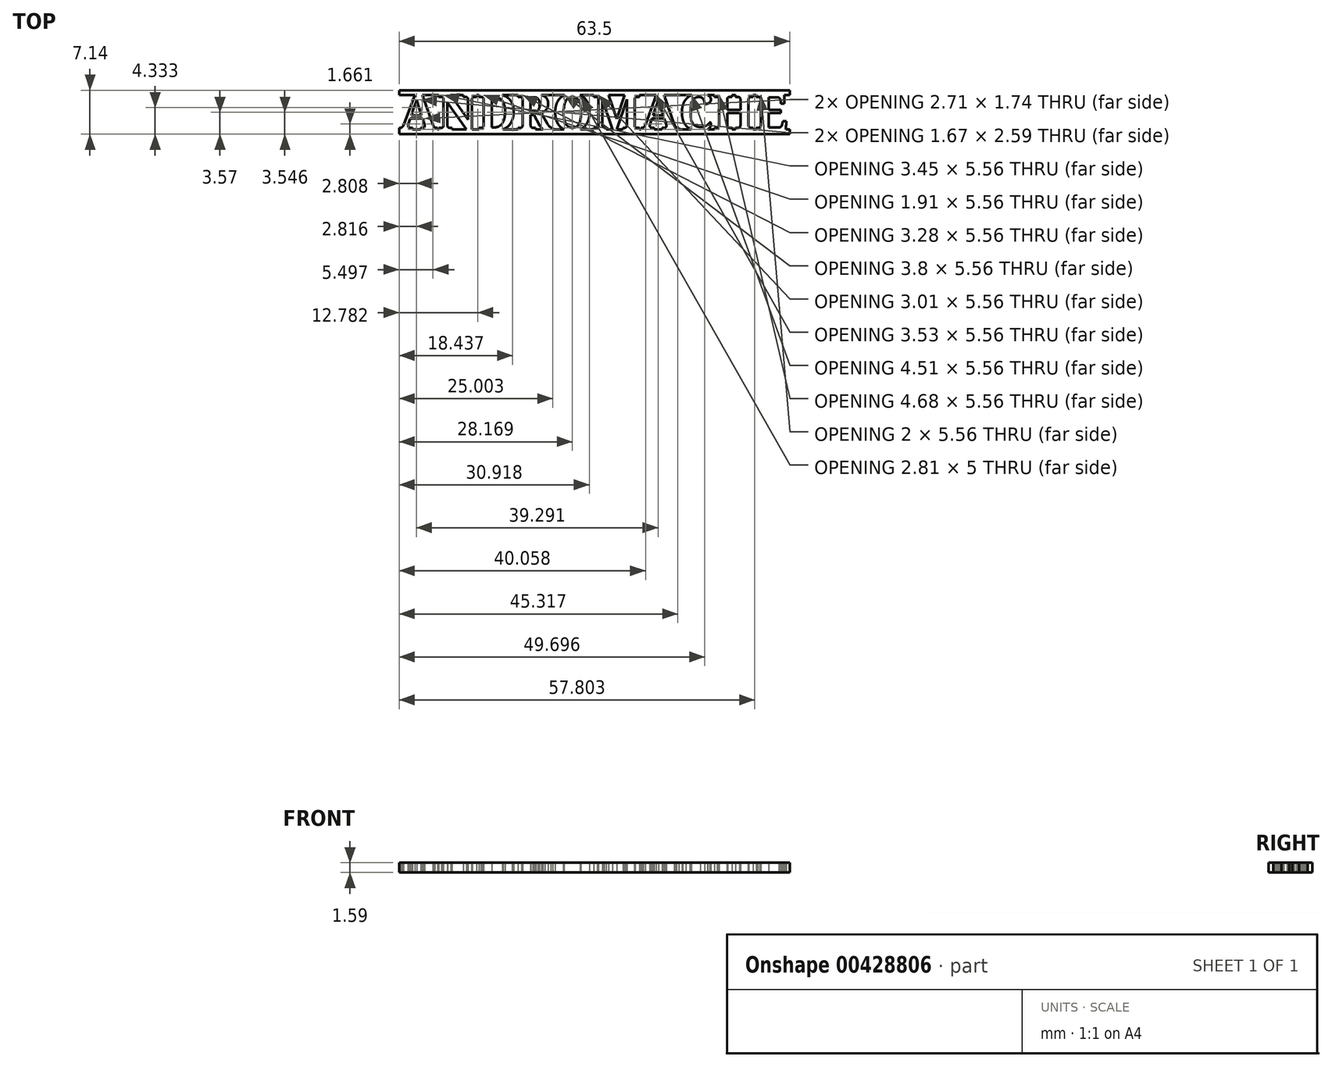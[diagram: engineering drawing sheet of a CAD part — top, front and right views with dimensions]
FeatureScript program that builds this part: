
annotation { "Feature Type Name" : "Feature", "Feature Type Description" : "" }
export const myFeature = defineFeature(function(context is Context, id is Id, definition is map)
    precondition{}
    {
        {
            var Q0;
            Q0=qCreatedBy(makeId("Top.planeOp"),FACE);
            var sketch = newSketch(context, id + "F0", { "sketchPlane" : qUnion([Q0])});
            skText(sketch, "E0", { "text": "ANDROMACHE", "fontName": "NotoSerif-Bold.ttf"});
            skLineSegment(sketch, "E1", {"start": v(31.75, 2.78) * mm, "end": v(31.75, 3.57) * mm});
            skLineSegment(sketch, "E2", {"start": v(31.75, 3.57) * mm, "end": v(-31.75, 3.57) * mm});
            skLineSegment(sketch, "E3", {"start": v(-31.75, 3.57) * mm, "end": v(-31.75, 2.78) * mm});
            skLineSegment(sketch, "E4.bottom", {"start": v(-31.75, -2.78) * mm, "end": v(31.75, -2.78) * mm});
            skLineSegment(sketch, "E4.top", {"start": v(-31.75, -3.57) * mm, "end": v(31.75, -3.57) * mm});
            skLineSegment(sketch, "E4.left", {"start": v(-31.75, -2.78) * mm, "end": v(-31.75, -3.57) * mm});
            skLineSegment(sketch, "E4.right", {"start": v(31.75, -2.78) * mm, "end": v(31.75, -3.57) * mm});
            skLineSegment(sketch, "E5", {"start": v(31.75, 2.78) * mm, "end": v(-31.75, 2.78) * mm});
            const initialGuessF0  = {"E0": [-0.03175, -0.00298, 1, 0, 0.00595]};
            skSetInitialGuess(sketch, initialGuessF0);
            skSolve(sketch);
        }
        {
            var Q0;
            {var subQ43=sQuery(id+"F0.wireOp",EDGE,"E0.sketch_text.stroke-17");Q0=makeQuery(id+"F0.imprint","IMPRINT",FACE,{"disambiguationData":[TD([[makeQuery(id+"F0.imprint","IMPRINT",EDGE,{"derivedFrom":subQ43}),1.0]])]});}
            var Q1;
            {var subQ0=sQuery(id+"F0.wireOp",EDGE,"E0.sketch_text.stroke-78");Q1=makeQuery(id+"F0.imprint","IMPRINT",FACE,{"disambiguationData":[TD([[makeQuery(id+"F0.imprint","IMPRINT",EDGE,{"derivedFrom":subQ0}),-1.0]])]});}
            var Q2;
            {var subQ7=sQuery(id+"F0.wireOp",EDGE,"E0.sketch_text.stroke-47");Q2=makeQuery(id+"F0.imprint","IMPRINT",FACE,{"disambiguationData":[TD([[makeQuery(id+"F0.imprint","IMPRINT",EDGE,{"derivedFrom":subQ7}),-1.0]])]});}
            var Q3;
            {var subQ0=sQuery(id+"F0.wireOp",EDGE,"E0.sketch_text.stroke-69");Q3=makeQuery(id+"F0.imprint","IMPRINT",FACE,{"disambiguationData":[TD([[makeQuery(id+"F0.imprint","IMPRINT",EDGE,{"derivedFrom":subQ0}),-1.0]])]});}
            var Q4;
            Q4=makeQuery(id+"F0.imprint","IMPRINT",FACE,{"disambiguationData":[TD([[makeQuery(id+"F0.imprint","IMPRINT",EDGE,{"derivedFrom":sQuery(id+"F0.wireOp",EDGE,"E0.sketch_text.stroke-0")}),-1.0]])]});
            var Q5;
            {var subQ0=sQuery(id+"F0.wireOp",EDGE,"E0.sketch_text.stroke-17");Q5=makeQuery(id+"F0.imprint","IMPRINT",FACE,{"disambiguationData":[TD([[makeQuery(id+"F0.imprint","IMPRINT",EDGE,{"derivedFrom":subQ0}),-1.0]])]});}
            var Q6;
            Q6=makeQuery(id+"F0.imprint","IMPRINT",FACE,{"disambiguationData":[TD([[makeQuery(id+"F0.imprint","IMPRINT",EDGE,{"derivedFrom":sQuery(id+"F0.wireOp",EDGE,"E4.top")}),1.0]])]});
            var Q7;
            Q7=makeQuery(id+"F0.imprint","IMPRINT",FACE,{"disambiguationData":[TD([[makeQuery(id+"F0.imprint","IMPRINT",EDGE,{"derivedFrom":sQuery(id+"F0.wireOp",EDGE,"E0.sketch_text.stroke-87")}),-1.0]])]});
            var Q8;
            {var subQ0=sQuery(id+"F0.wireOp",EDGE,"E0.sketch_text.stroke-105");Q8=makeQuery(id+"F0.imprint","IMPRINT",FACE,{"disambiguationData":[TD([[makeQuery(id+"F0.imprint","IMPRINT",EDGE,{"derivedFrom":subQ0}),-1.0]])]});}
            var Q9;
            Q9=makeQuery(id+"F0.imprint","IMPRINT",FACE,{"disambiguationData":[TD([[makeQuery(id+"F0.imprint","IMPRINT",EDGE,{"derivedFrom":sQuery(id+"F0.wireOp",EDGE,"E0.sketch_text.stroke-119")}),-1.0]])]});
            var Q10;
            Q10=makeQuery(id+"F0.imprint","IMPRINT",FACE,{"disambiguationData":[TD([[makeQuery(id+"F0.imprint","IMPRINT",EDGE,{"derivedFrom":sQuery(id+"F0.wireOp",EDGE,"E0.sketch_text.stroke-172")}),-1.0]])]});
            var Q11;
            {var subQ0=sQuery(id+"F0.wireOp",EDGE,"E0.sketch_text.stroke-131");Q11=makeQuery(id+"F0.imprint","IMPRINT",FACE,{"disambiguationData":[TD([[makeQuery(id+"F0.imprint","IMPRINT",EDGE,{"derivedFrom":subQ0}),-1.0]])]});}
            var Q12;
            {var subQ0=sQuery(id+"F0.wireOp",EDGE,"E0.sketch_text.stroke-184");var subQ1=sQuery(id+"F0.wireOp",EDGE,"E0.sketch_text.stroke-183");var subQ2=makeQuery(id+"F0.imprint","INTERSECT",VERTEX,{"derivedFrom":[subQ1,subQ0]});Q12=makeQuery(id+"F0.imprint","IMPRINT",FACE,{"disambiguationData":[TD([[makeQuery(id+"F0.imprint","IMPRINT",EDGE,{"disambiguationData":[TD([[subQ2,1.0]])],"derivedFrom":subQ1}),-1.0]])]});}
            var Q13;
            {var subQ0=sQuery(id+"F0.wireOp",EDGE,"E0.sketch_text.stroke-176");var subQ1=sQuery(id+"F0.wireOp",EDGE,"E0.sketch_text.stroke-175");var subQ2=makeQuery(id+"F0.imprint","INTERSECT",VERTEX,{"derivedFrom":[subQ1,subQ0]});Q13=makeQuery(id+"F0.imprint","IMPRINT",FACE,{"disambiguationData":[TD([[makeQuery(id+"F0.imprint","IMPRINT",EDGE,{"disambiguationData":[TD([[subQ2,1.0]])],"derivedFrom":subQ1}),-1.0]])]});}
            var Q14;
            {var subQ15=sQuery(id+"F0.wireOp",EDGE,"E0.sketch_text.stroke-204");Q14=makeQuery(id+"F0.imprint","IMPRINT",FACE,{"disambiguationData":[TD([[makeQuery(id+"F0.imprint","IMPRINT",EDGE,{"derivedFrom":subQ15}),-1.0]])]});}
            var Q15;
            Q15=makeQuery(id+"F0.imprint","IMPRINT",FACE,{"disambiguationData":[TD([[makeQuery(id+"F0.imprint","IMPRINT",EDGE,{"derivedFrom":sQuery(id+"F0.wireOp",EDGE,"E0.sketch_text.stroke-253")}),-1.0]])]});
            var Q16;
            Q16=makeQuery(id+"F0.imprint","IMPRINT",FACE,{"disambiguationData":[TD([[makeQuery(id+"F0.imprint","IMPRINT",EDGE,{"derivedFrom":sQuery(id+"F0.wireOp",EDGE,"E0.sketch_text.stroke-300")}),-1.0]])]});
            var Q17;
            {var subQ7=sQuery(id+"F0.wireOp",EDGE,"E0.sketch_text.stroke-338");Q17=makeQuery(id+"F0.imprint","IMPRINT",FACE,{"disambiguationData":[TD([[makeQuery(id+"F0.imprint","IMPRINT",EDGE,{"derivedFrom":subQ7}),-1.0]])]});}
            var Q18;
            Q18=makeQuery(id+"F0.imprint","IMPRINT",FACE,{"disambiguationData":[TD([[makeQuery(id+"F0.imprint","IMPRINT",EDGE,{"derivedFrom":sQuery(id+"F0.wireOp",EDGE,"E0.sketch_text.stroke-398")}),-1.0]])]});
            var Q19;
            {var subQ0=sQuery(id+"F0.wireOp",EDGE,"E0.sketch_text.stroke-420");Q19=makeQuery(id+"F0.imprint","IMPRINT",FACE,{"disambiguationData":[TD([[makeQuery(id+"F0.imprint","IMPRINT",EDGE,{"derivedFrom":subQ0}),-1.0]])]});}
            var Q20;
            {var subQ0=sQuery(id+"F0.wireOp",EDGE,"E0.sketch_text.stroke-383");Q20=makeQuery(id+"F0.imprint","IMPRINT",FACE,{"disambiguationData":[TD([[makeQuery(id+"F0.imprint","IMPRINT",EDGE,{"derivedFrom":subQ0}),-1.0]])]});}
            var Q21;
            {var subQ0=sQuery(id+"F0.wireOp",EDGE,"E0.sketch_text.stroke-367");Q21=makeQuery(id+"F0.imprint","IMPRINT",FACE,{"disambiguationData":[TD([[makeQuery(id+"F0.imprint","IMPRINT",EDGE,{"derivedFrom":subQ0}),-1.0]])]});}
            var Q22;
            {var subQ0=sQuery(id+"F0.wireOp",EDGE,"E0.sketch_text.stroke-270");Q22=makeQuery(id+"F0.imprint","IMPRINT",FACE,{"disambiguationData":[TD([[makeQuery(id+"F0.imprint","IMPRINT",EDGE,{"derivedFrom":subQ0}),-1.0]])]});}
            var Q23;
            {var subQ0=sQuery(id+"F0.wireOp",EDGE,"E0.sketch_text.stroke-318");Q23=makeQuery(id+"F0.imprint","IMPRINT",FACE,{"disambiguationData":[TD([[makeQuery(id+"F0.imprint","IMPRINT",EDGE,{"derivedFrom":subQ0}),-1.0]])]});}
            var Q24;
            {var subQ0=sQuery(id+"F0.wireOp",EDGE,"E0.sketch_text.stroke-235");Q24=makeQuery(id+"F0.imprint","IMPRINT",FACE,{"disambiguationData":[TD([[makeQuery(id+"F0.imprint","IMPRINT",EDGE,{"derivedFrom":subQ0}),-1.0]])]});}
            var Q25;
            {var subQ0=sQuery(id+"F0.wireOp",EDGE,"E0.sketch_text.stroke-238");Q25=makeQuery(id+"F0.imprint","IMPRINT",FACE,{"disambiguationData":[TD([[makeQuery(id+"F0.imprint","IMPRINT",EDGE,{"derivedFrom":subQ0}),-1.0]])]});}
            var Q26;
            {var subQ0=sQuery(id+"F0.wireOp",EDGE,"E0.sketch_text.stroke-159");Q26=makeQuery(id+"F0.imprint","IMPRINT",FACE,{"disambiguationData":[TD([[makeQuery(id+"F0.imprint","IMPRINT",EDGE,{"derivedFrom":subQ0}),-1.0]])]});}
            var Q27;
            {var subQ6=sQuery(id+"F0.wireOp",EDGE,"E0.sketch_text.stroke-145");Q27=makeQuery(id+"F0.imprint","IMPRINT",FACE,{"disambiguationData":[TD([[makeQuery(id+"F0.imprint","IMPRINT",EDGE,{"derivedFrom":subQ6}),-1.0]])]});}
            var Q28;
            {var subQ0=sQuery(id+"F0.wireOp",EDGE,"E0.sketch_text.stroke-91");Q28=makeQuery(id+"F0.imprint","IMPRINT",FACE,{"disambiguationData":[TD([[makeQuery(id+"F0.imprint","IMPRINT",EDGE,{"derivedFrom":subQ0}),-1.0]])]});}
            var Q29;
            {var subQ1=sQuery(id+"F0.wireOp",EDGE,"E0.sketch_text.stroke-48");Q29=makeQuery(id+"F0.imprint","IMPRINT",FACE,{"disambiguationData":[TD([[makeQuery(id+"F0.imprint","IMPRINT",EDGE,{"derivedFrom":subQ1}),-1.0]])]});}
            var Q30;
            {var subQ0=sQuery(id+"F0.wireOp",EDGE,"E0.sketch_text.stroke-25");Q30=makeQuery(id+"F0.imprint","IMPRINT",FACE,{"disambiguationData":[TD([[makeQuery(id+"F0.imprint","IMPRINT",EDGE,{"derivedFrom":subQ0}),-1.0]])]});}
            var Q31;
            {var subQ0=sQuery(id+"F0.wireOp",EDGE,"E0.sketch_text.stroke-55");Q31=makeQuery(id+"F0.imprint","IMPRINT",FACE,{"disambiguationData":[TD([[makeQuery(id+"F0.imprint","IMPRINT",EDGE,{"derivedFrom":subQ0}),-1.0]])]});}
            var Q32;
            {var subQ0=sQuery(id+"F0.wireOp",EDGE,"E0.sketch_text.stroke-9");Q32=makeQuery(id+"F0.imprint","IMPRINT",FACE,{"disambiguationData":[TD([[makeQuery(id+"F0.imprint","IMPRINT",EDGE,{"derivedFrom":subQ0}),-1.0]])]});}
            var Q33;
            {var subQ0=sQuery(id+"F0.wireOp",EDGE,"E0.sketch_text.stroke-221");Q33=makeQuery(id+"F0.imprint","IMPRINT",FACE,{"disambiguationData":[TD([[makeQuery(id+"F0.imprint","IMPRINT",EDGE,{"derivedFrom":subQ0}),-1.0]])]});}
            var Q34;
            {var subQ26=sQuery(id+"F0.wireOp",EDGE,"E0.sketch_text.stroke-205");Q34=makeQuery(id+"F0.imprint","IMPRINT",FACE,{"disambiguationData":[TD([[makeQuery(id+"F0.imprint","IMPRINT",EDGE,{"derivedFrom":subQ26}),-1.0]])]});}
            var Q35;
            {var subQ0=sQuery(id+"F0.wireOp",EDGE,"E0.sketch_text.stroke-212");Q35=makeQuery(id+"F0.imprint","IMPRINT",FACE,{"disambiguationData":[TD([[makeQuery(id+"F0.imprint","IMPRINT",EDGE,{"derivedFrom":subQ0}),-1.0]])]});}
            var Q36;
            {var subQ0=sQuery(id+"F0.wireOp",EDGE,"E0.sketch_text.stroke-262");Q36=makeQuery(id+"F0.imprint","IMPRINT",FACE,{"disambiguationData":[TD([[makeQuery(id+"F0.imprint","IMPRINT",EDGE,{"derivedFrom":subQ0}),-1.0]])]});}
            var Q37;
            {var subQ0=sQuery(id+"F0.wireOp",EDGE,"E0.sketch_text.stroke-278");Q37=makeQuery(id+"F0.imprint","IMPRINT",FACE,{"disambiguationData":[TD([[makeQuery(id+"F0.imprint","IMPRINT",EDGE,{"derivedFrom":subQ0}),-1.0]])]});}
            var Q38;
            {var subQ4=sQuery(id+"F0.wireOp",EDGE,"E0.sketch_text.stroke-309");Q38=makeQuery(id+"F0.imprint","IMPRINT",FACE,{"disambiguationData":[TD([[makeQuery(id+"F0.imprint","IMPRINT",EDGE,{"derivedFrom":subQ4}),-1.0]])]});}
            var Q39;
            {var subQ22=sQuery(id+"F0.wireOp",EDGE,"E0.sketch_text.stroke-339");Q39=makeQuery(id+"F0.imprint","IMPRINT",FACE,{"disambiguationData":[TD([[makeQuery(id+"F0.imprint","IMPRINT",EDGE,{"derivedFrom":subQ22}),-1.0]])]});}
            var Q40;
            {var subQ0=sQuery(id+"F0.wireOp",EDGE,"E0.sketch_text.stroke-353");Q40=makeQuery(id+"F0.imprint","IMPRINT",FACE,{"disambiguationData":[TD([[makeQuery(id+"F0.imprint","IMPRINT",EDGE,{"derivedFrom":subQ0}),-1.0]])]});}
            var Q41;
            {var subQ0=sQuery(id+"F0.wireOp",EDGE,"E0.sketch_text.stroke-406");Q41=makeQuery(id+"F0.imprint","IMPRINT",FACE,{"disambiguationData":[TD([[makeQuery(id+"F0.imprint","IMPRINT",EDGE,{"derivedFrom":subQ0}),-1.0]])]});}
            extrude(context, id + "F1", {"entities" : qUnion([Q0, Q1, Q2, Q3, Q4, Q5, Q6, Q7, Q8, Q9, Q10, Q11, Q12, Q13, Q14, Q15, Q16, Q17, Q18, Q19, Q20, Q21, Q22, Q23, Q24, Q25, Q26, Q27, Q28, Q29, Q30, Q31, Q32, Q33, Q34, Q35, Q36, Q37, Q38, Q39, Q40, Q41]), "depth" : 1.59 * mm});
        }
    });
